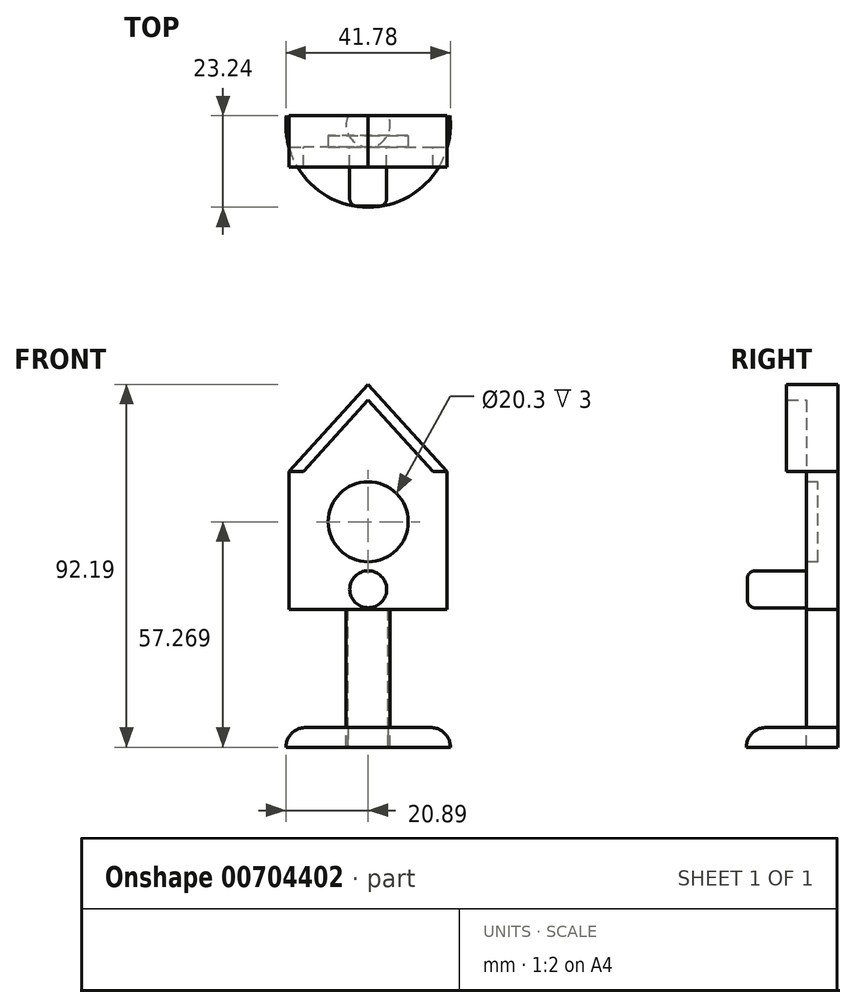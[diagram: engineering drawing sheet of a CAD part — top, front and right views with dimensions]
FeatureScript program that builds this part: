
annotation { "Feature Type Name" : "Feature", "Feature Type Description" : "" }
export const myFeature = defineFeature(function(context is Context, id is Id, definition is map)
    precondition{}
    {
        {
            var Q0;
            Q0=qCreatedBy(makeId("Front.planeOp"),FACE);
            var sketch = newSketch(context, id + "F0", { "sketchPlane" : qUnion([Q0])});
            skLineSegment(sketch, "E0.bottom", {"start": v(0, 0) * mm, "end": v(-20.06, 0) * mm});
            skLineSegment(sketch, "E0.top", {"start": v(0, 35.05) * mm, "end": v(-20.06, 35.05) * mm});
            skLineSegment(sketch, "E0.left", {"start": v(0, 0) * mm, "end": v(0, 35.05) * mm});
            skLineSegment(sketch, "E0.right", {"start": v(-20.06, 0) * mm, "end": v(-20.06, 35.05) * mm});
            skLineSegment(sketch, "E1", {"start": v(-20.06, 35.05) * mm, "end": v(0, 57.19) * mm});
            skLineSegment(sketch, "E2", {"start": v(0, 57.19) * mm, "end": v(0, 35.05) * mm});
            skLineSegment(sketch, "E3.MirrorCS", {"start": v(20.06, 35.05) * mm, "end": v(0, 57.19) * mm});
            skLineSegment(sketch, "E4.MirrorCS", {"start": v(0, 35.05) * mm, "end": v(20.06, 35.05) * mm});
            skLineSegment(sketch, "E5.MirrorCS", {"start": v(0, 0) * mm, "end": v(20.06, 0) * mm});
            skLineSegment(sketch, "E6.MirrorCS", {"start": v(20.06, 0) * mm, "end": v(20.06, 35.05) * mm});
            skSolve(sketch);
        }
        {
            var Q0;
            Q0=makeQuery(id+"F0.imprint","IMPRINT",FACE,{"disambiguationData":[TD([[makeQuery(id+"F0.imprint","IMPRINT",EDGE,{"derivedFrom":sQuery(id+"F0.wireOp",EDGE,"E2")}),1.0]])]});
            var Q1;
            Q1=makeQuery(id+"F0.imprint","IMPRINT",FACE,{"disambiguationData":[TD([[makeQuery(id+"F0.imprint","IMPRINT",EDGE,{"derivedFrom":sQuery(id+"F0.wireOp",EDGE,"E0.top")}),-1.0]])]});
            var Q2;
            Q2=makeQuery(id+"F0.imprint","IMPRINT",FACE,{"disambiguationData":[TD([[makeQuery(id+"F0.imprint","IMPRINT",EDGE,{"derivedFrom":sQuery(id+"F0.wireOp",EDGE,"E0.bottom")}),-1.0]])]});
            var Q3;
            Q3=makeQuery(id+"F0.imprint","IMPRINT",FACE,{"disambiguationData":[TD([[makeQuery(id+"F0.imprint","IMPRINT",EDGE,{"derivedFrom":sQuery(id+"F0.wireOp",EDGE,"E0.left")}),-1.0]])]});
            extrude(context, id + "F1", {"entities" : qUnion([Q0, Q1, Q2, Q3]), "depth" : 8 * mm, "offsetDistance" : 25 * mm});
        }
        {
            var Q0;
            Q0=makeQuery(id+"F1.opExtrude","CAP_FACE",FACE,{"disambiguationData":[OSD([sQuery(id+"F0.wireOp",EDGE,"E0.bottom"),sQuery(id+"F0.wireOp",EDGE,"E0.right"),sQuery(id+"F0.wireOp",EDGE,"E1"),sQuery(id+"F0.wireOp",EDGE,"E3.MirrorCS"),sQuery(id+"F0.wireOp",EDGE,"E5.MirrorCS"),sQuery(id+"F0.wireOp",EDGE,"E6.MirrorCS")])],"isStart":false});
            var sketch = newSketch(context, id + "F2", { "sketchPlane" : qUnion([Q0])});
            skCircle(sketch, "E7", {"center": v(0, 22.27) * mm, "radius": 10.15 * mm});
            skSolve(sketch);
        }
        {
            var Q0;
            Q0=makeQuery(id+"F2.imprint","IMPRINT",FACE,{"disambiguationData":[TD([[makeQuery(id+"F2.imprint","IMPRINT",EDGE,{"derivedFrom":sQuery(id+"F2.wireOp",EDGE,"E7")}),1.0]])]});
            extrude(context, id + "F3", {"entities" : qUnion([Q0]), "operationType" : NewBodyOperationType.REMOVE, "oppositeDirection" : true, "depth" : 3 * mm, "offsetDistance" : 25 * mm});
        }
        {
            var Q0;
            Q0=makeQuery(id+"F1.opExtrude","CAP_FACE",FACE,{"disambiguationData":[OSD([sQuery(id+"F0.wireOp",EDGE,"E0.bottom"),sQuery(id+"F0.wireOp",EDGE,"E0.right"),sQuery(id+"F0.wireOp",EDGE,"E1"),sQuery(id+"F0.wireOp",EDGE,"E3.MirrorCS"),sQuery(id+"F0.wireOp",EDGE,"E5.MirrorCS"),sQuery(id+"F0.wireOp",EDGE,"E6.MirrorCS")])],"isStart":false});
            var sketch = newSketch(context, id + "F4", { "sketchPlane" : qUnion([Q0])});
            skCircle(sketch, "E8", {"center": v(0, 5.12) * mm, "radius": 4.7 * mm});
            skSolve(sketch);
        }
        {
            var Q0;
            Q0=makeQuery(id+"F4.imprint","IMPRINT",FACE,{"disambiguationData":[TD([[makeQuery(id+"F4.imprint","IMPRINT",EDGE,{"derivedFrom":sQuery(id+"F4.wireOp",EDGE,"E8")}),1.0]])]});
            extrude(context, id + "F5", {"entities" : qUnion([Q0]), "operationType" : NewBodyOperationType.ADD, "depth" : 15 * mm, "offsetDistance" : 25 * mm});
        }
        {
            var Q0;
            Q0=makeQuery(id+"F5.opExtrude","CAP_EDGE",EDGE,{"disambiguationData":[OSD([sQuery(id+"F4.wireOp",EDGE,"E8")])],"isStart":false});
            fillet(context, id + "F6", {"entities" : qUnion([Q0]), "radius" : 2 * mm, "tangentPropagation" : true, "allowEdgeOverflow" : false});
        }
        {
            var Q0;
            Q0=makeQuery(id+"F1.opExtrude","SWEPT_FACE",FACE,{"disambiguationData":[OSD([sQuery(id+"F0.wireOp",EDGE,"E0.bottom"),sQuery(id+"F0.wireOp",EDGE,"E5.MirrorCS")])]});
            var sketch = newSketch(context, id + "F7", { "sketchPlane" : qUnion([Q0])});
            skArc(sketch, "E9", {"start": v(5.08, 0) * mm, "mid": v(0, 7.95) * mm, "end": v(-5.08, 0) * mm});
            skLineSegment(sketch, "E10", {"start": v(-5.08, 0) * mm, "end": v(5.08, 0) * mm});
            skSolve(sketch);
        }
        {
            var Q0;
            Q0=makeQuery(id+"F7.imprint","IMPRINT",FACE,{"disambiguationData":[TD([[makeQuery(id+"F7.imprint","IMPRINT",EDGE,{"derivedFrom":sQuery(id+"F7.wireOp",EDGE,"E9")}),1.0]])]});
            extrude(context, id + "F8", {"entities" : qUnion([Q0]), "operationType" : NewBodyOperationType.ADD, "depth" : 35 * mm, "offsetDistance" : 25 * mm});
        }
        {
            var Q0;
            Q0=makeQuery(id+"F8.opExtrude","CAP_FACE",FACE,{"disambiguationData":[OSD([sQuery(id+"F7.wireOp",EDGE,"E9"),sQuery(id+"F7.wireOp",EDGE,"E10")])],"isStart":false});
            var sketch = newSketch(context, id + "F9", { "sketchPlane" : qUnion([Q0])});
            skArc(sketch, "E11", {"start": v(20.76, 0) * mm, "mid": v(0, 23.24) * mm, "end": v(-20.76, 0) * mm});
            skLineSegment(sketch, "E12", {"start": v(-20.76, 0) * mm, "end": v(20.76, 0) * mm});
            skSolve(sketch);
        }
        {
            var Q0;
            {var subQ0=sQuery(id+"F9.wireOp",EDGE,"E11");Q0=makeQuery(id+"F9.imprint","IMPRINT",FACE,{"disambiguationData":[TD([[makeQuery(id+"F9.imprint","IMPRINT",EDGE,{"derivedFrom":subQ0}),1.0]])]});}
            extrude(context, id + "F10", {"entities" : qUnion([Q0]), "oppositeDirection" : true, "depth" : 5 * mm, "offsetDistance" : 25 * mm});
        }
        {
            var Q0;
            Q0=makeQuery(id+"F10.opExtrude","CAP_EDGE",EDGE,{"disambiguationData":[OSD([sQuery(id+"F9.wireOp",EDGE,"E11")])],"isStart":false});
            fillet(context, id + "F11", {"entities" : qUnion([Q0]), "radius" : 5 * mm, "tangentPropagation" : true, "allowEdgeOverflow" : false});
        }
        {
            var Q0;
            Q0=makeQuery(id+"F1.opExtrude","CAP_FACE",FACE,{"disambiguationData":[OSD([sQuery(id+"F0.wireOp",EDGE,"E0.bottom"),sQuery(id+"F0.wireOp",EDGE,"E0.right"),sQuery(id+"F0.wireOp",EDGE,"E1"),sQuery(id+"F0.wireOp",EDGE,"E3.MirrorCS"),sQuery(id+"F0.wireOp",EDGE,"E5.MirrorCS"),sQuery(id+"F0.wireOp",EDGE,"E6.MirrorCS")])],"isStart":false});
            var sketch = newSketch(context, id + "F12", { "sketchPlane" : qUnion([Q0])});
            skLineSegment(sketch, "E13", {"start": v(-20.06, 35.05) * mm, "end": v(-16.44, 35.05) * mm});
            skLineSegment(sketch, "E14", {"start": v(0, 53.19) * mm, "end": v(-16.44, 35.05) * mm});
            skLineSegment(sketch, "E15", {"start": v(0, 53.19) * mm, "end": v(16.44, 35.05) * mm});
            skLineSegment(sketch, "E16.trimOffspring", {"start": v(16.44, 35.05) * mm, "end": v(20.06, 35.05) * mm});
            skSolve(sketch);
        }
        {
            var Q0;
            Q0=makeQuery(id+"F12.imprint","IMPRINT",FACE,{"disambiguationData":[TD([[makeQuery(id+"F12.imprint","IMPRINT",EDGE,{"derivedFrom":sQuery(id+"F12.wireOp",EDGE,"E13")}),1.0]])]});
            extrude(context, id + "F13", {"entities" : qUnion([Q0]), "operationType" : NewBodyOperationType.ADD, "depth" : 5 * mm, "offsetDistance" : 25 * mm});
        }
    });
